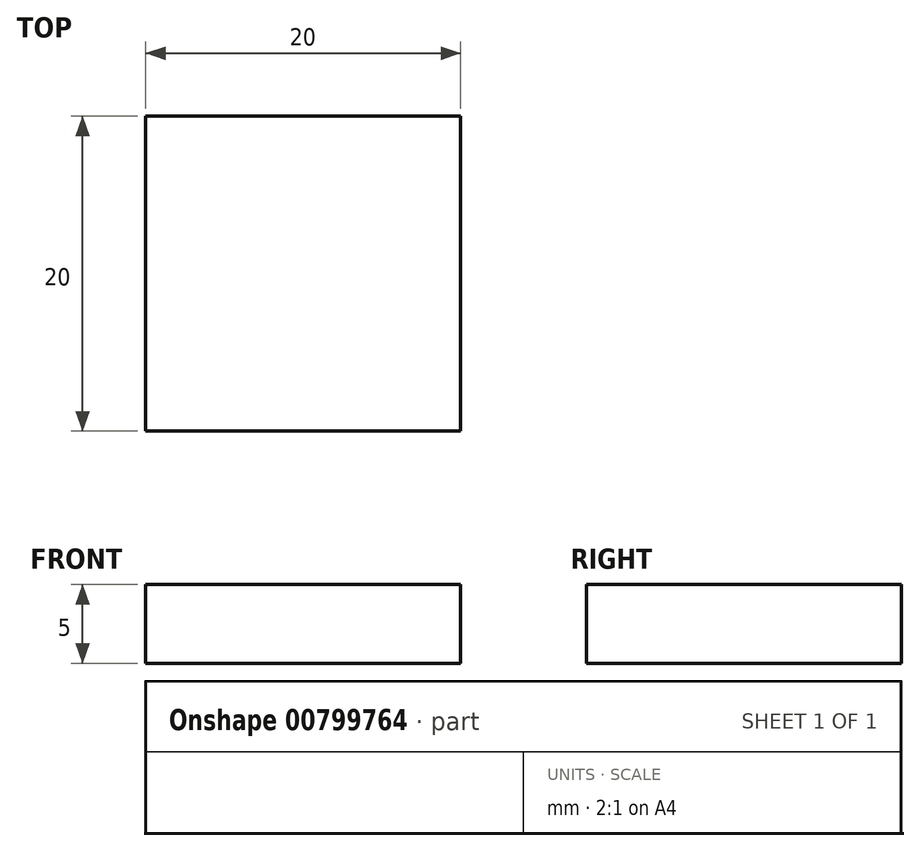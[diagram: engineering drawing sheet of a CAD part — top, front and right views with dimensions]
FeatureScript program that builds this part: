
annotation { "Feature Type Name" : "Feature", "Feature Type Description" : "" }
export const myFeature = defineFeature(function(context is Context, id is Id, definition is map)
    precondition{}
    {
        {
            var Q0;
            Q0=qCreatedBy(makeId("Top.planeOp"),FACE);
            var sketch = newSketch(context, id + "F0", { "sketchPlane" : qUnion([Q0])});
            skLineSegment(sketch, "E0.bottom", {"start": v(0, 0) * mm, "end": v(20, 0) * mm});
            skLineSegment(sketch, "E0.top", {"start": v(0, 20) * mm, "end": v(20, 20) * mm});
            skLineSegment(sketch, "E0.left", {"start": v(0, 0) * mm, "end": v(0, 20) * mm});
            skLineSegment(sketch, "E0.right", {"start": v(20, 0) * mm, "end": v(20, 20) * mm});
            skSolve(sketch);
        }
        {
            var Q0;
            Q0 = qSketchRegion(id + "F0", true);
            extrude(context, id + "F1", {"entities" : qUnion([Q0]), "depth" : 5 * mm, "offsetDistance" : 25 * mm});
        }
    });
